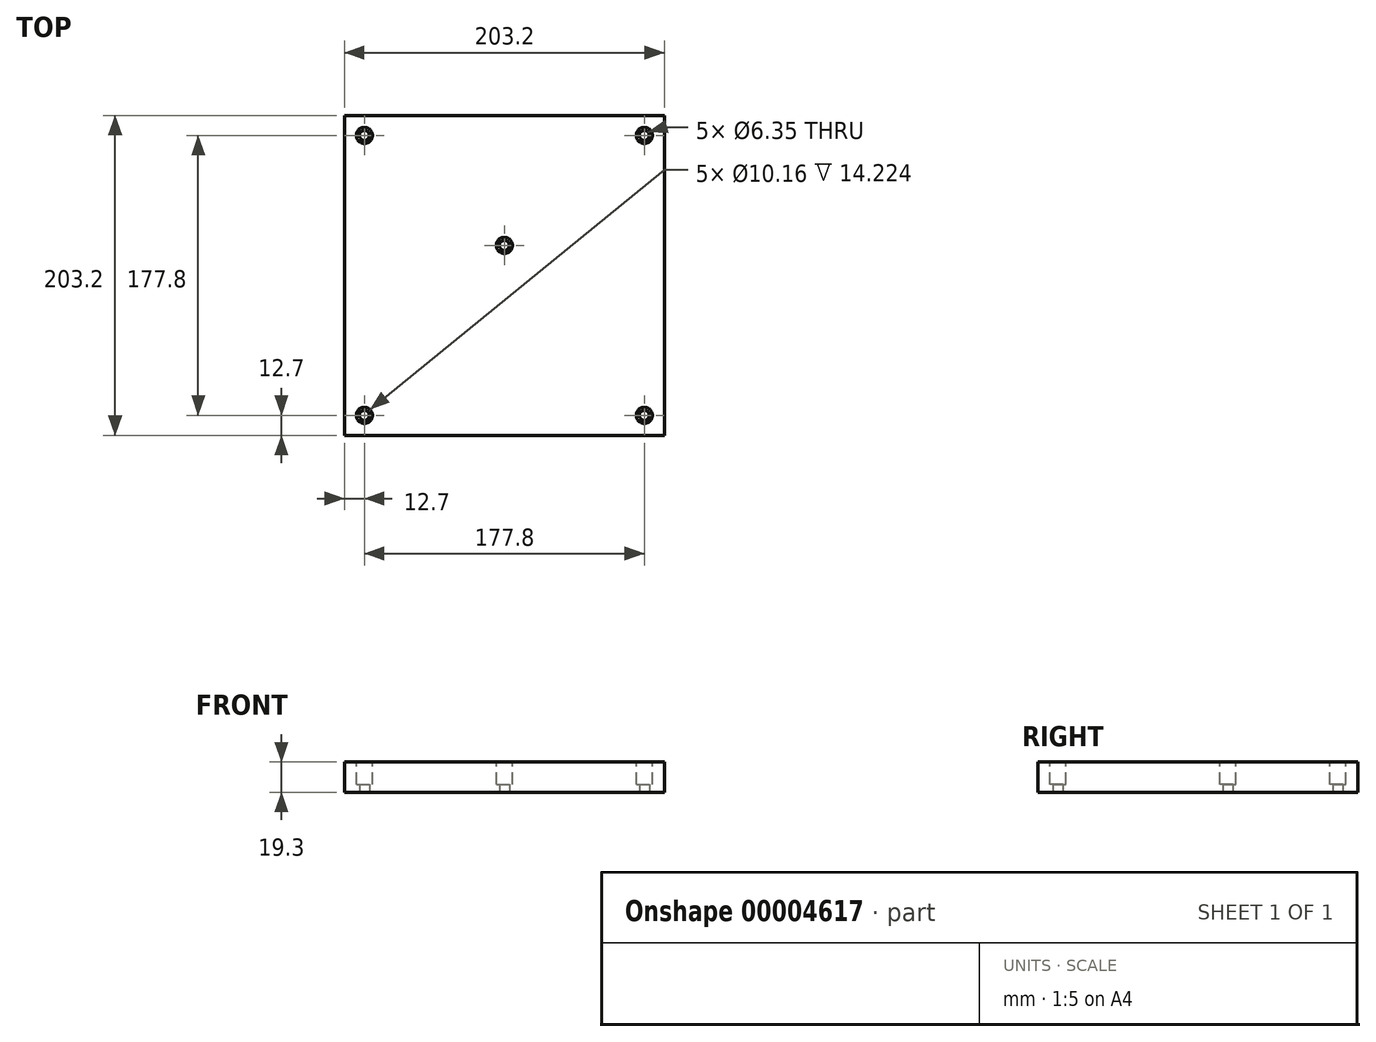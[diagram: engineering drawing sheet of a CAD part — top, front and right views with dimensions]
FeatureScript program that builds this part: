
annotation { "Feature Type Name" : "Feature", "Feature Type Description" : "" }
export const myFeature = defineFeature(function(context is Context, id is Id, definition is map)
    precondition{}
    {
        {
            var Q0;
            Q0=qCreatedBy(makeId("Top.planeOp"),FACE);
            var sketch = newSketch(context, id + "F0", { "sketchPlane" : qUnion([Q0])});
            skLineSegment(sketch, "E0.rect.bottom", {"start": v(101.6, -101.6) * mm, "end": v(-101.6, -101.6) * mm});
            skLineSegment(sketch, "E0.rect.top", {"start": v(101.6, 101.6) * mm, "end": v(-101.6, 101.6) * mm});
            skLineSegment(sketch, "E0.rect.left", {"start": v(101.6, -101.6) * mm, "end": v(101.6, 101.6) * mm});
            skLineSegment(sketch, "E0.rect.right", {"start": v(-101.6, -101.6) * mm, "end": v(-101.6, 101.6) * mm});
            skPoint(sketch, "E0.rect.middle", {"position": v(0, 0) * mm});
            skCircle(sketch, "E1", {"center": v(88.9, 88.9) * mm, "radius": 3.18 * mm});
            skCircle(sketch, "E2", {"center": v(-88.9, 88.9) * mm, "radius": 3.18 * mm});
            skCircle(sketch, "E3", {"center": v(-88.9, -88.9) * mm, "radius": 3.18 * mm});
            skCircle(sketch, "E4", {"center": v(88.9, -88.9) * mm, "radius": 3.18 * mm});
            skLineSegment(sketch, "E5.rect.bottom", {"start": v(88.9, 88.9) * mm, "end": v(-88.9, 88.9) * mm, "construction": true});
            skLineSegment(sketch, "E5.rect.top", {"start": v(88.9, -88.9) * mm, "end": v(-88.9, -88.9) * mm, "construction": true});
            skLineSegment(sketch, "E5.rect.left", {"start": v(88.9, 88.9) * mm, "end": v(88.9, -88.9) * mm, "construction": true});
            skLineSegment(sketch, "E5.rect.right", {"start": v(-88.9, 88.9) * mm, "end": v(-88.9, -88.9) * mm, "construction": true});
            skCircle(sketch, "E6", {"center": v(0, 19.05) * mm, "radius": 3.18 * mm});
            skSolve(sketch);
        }
        {
            var Q0;
            Q0 = qSketchRegion(id + "F0", true);
            extrude(context, id + "F1", {"entities" : qUnion([Q0]), "depth" : 19.3 * mm});
        }
        {
            var Q0;
            Q0=makeQuery(id+"F1.opExtrude","CAP_FACE",FACE,{"disambiguationData":[OSD([sQuery(id+"F0.wireOp",EDGE,"E0.rect.bottom"),sQuery(id+"F0.wireOp",EDGE,"E0.rect.top"),sQuery(id+"F0.wireOp",EDGE,"E0.rect.left"),sQuery(id+"F0.wireOp",EDGE,"E0.rect.right"),sQuery(id+"F0.wireOp",EDGE,"E1"),sQuery(id+"F0.wireOp",EDGE,"E2"),sQuery(id+"F0.wireOp",EDGE,"E3"),sQuery(id+"F0.wireOp",EDGE,"E4"),sQuery(id+"F0.wireOp",EDGE,"E6")])],"isStart":false});
            var sketch = newSketch(context, id + "F2", { "sketchPlane" : qUnion([Q0])});
            skCircle(sketch, "E7", {"center": v(-88.9, 88.9) * mm, "radius": 5.08 * mm});
            skCircle(sketch, "E8", {"center": v(0, 19.05) * mm, "radius": 5.08 * mm});
            skCircle(sketch, "E9", {"center": v(88.9, 88.9) * mm, "radius": 5.08 * mm});
            skCircle(sketch, "E10", {"center": v(-88.9, -88.9) * mm, "radius": 5.08 * mm});
            skCircle(sketch, "E11", {"center": v(88.9, -88.9) * mm, "radius": 5.08 * mm});
            skSolve(sketch);
        }
        {
            var Q0;
            Q0=makeQuery(id+"F1.opExtrude","CAP_FACE",FACE,{"disambiguationData":[OSD([sQuery(id+"F0.wireOp",EDGE,"E0.rect.bottom"),sQuery(id+"F0.wireOp",EDGE,"E0.rect.top"),sQuery(id+"F0.wireOp",EDGE,"E0.rect.left"),sQuery(id+"F0.wireOp",EDGE,"E0.rect.right"),sQuery(id+"F0.wireOp",EDGE,"E1"),sQuery(id+"F0.wireOp",EDGE,"E2"),sQuery(id+"F0.wireOp",EDGE,"E3"),sQuery(id+"F0.wireOp",EDGE,"E4"),sQuery(id+"F0.wireOp",EDGE,"E6")])],"isStart":true});
            cPlane(context, id + "F3", {"entities" : qUnion([Q0]), "cplaneType" : CPlaneType.OFFSET, "offset" : 5.08 * mm, "oppositeDirection" : true, "width" : 152.4 * mm, "height" : 152.4 * mm});
        }
        {
            var Q0;
            Q0 = qSketchRegion(id + "F2", true);
            var Q1;
            Q1=qCreatedBy(id+"F3.planeOp",FACE);
            extrude(context, id + "F4", {"entities" : qUnion([Q0]), "operationType" : NewBodyOperationType.REMOVE, "endBound" : BoundingType.UP_TO_SURFACE, "oppositeDirection" : true, "endBoundEntityFace" : qUnion([Q1]), "depth" : 25.4 * mm});
        }
    });
